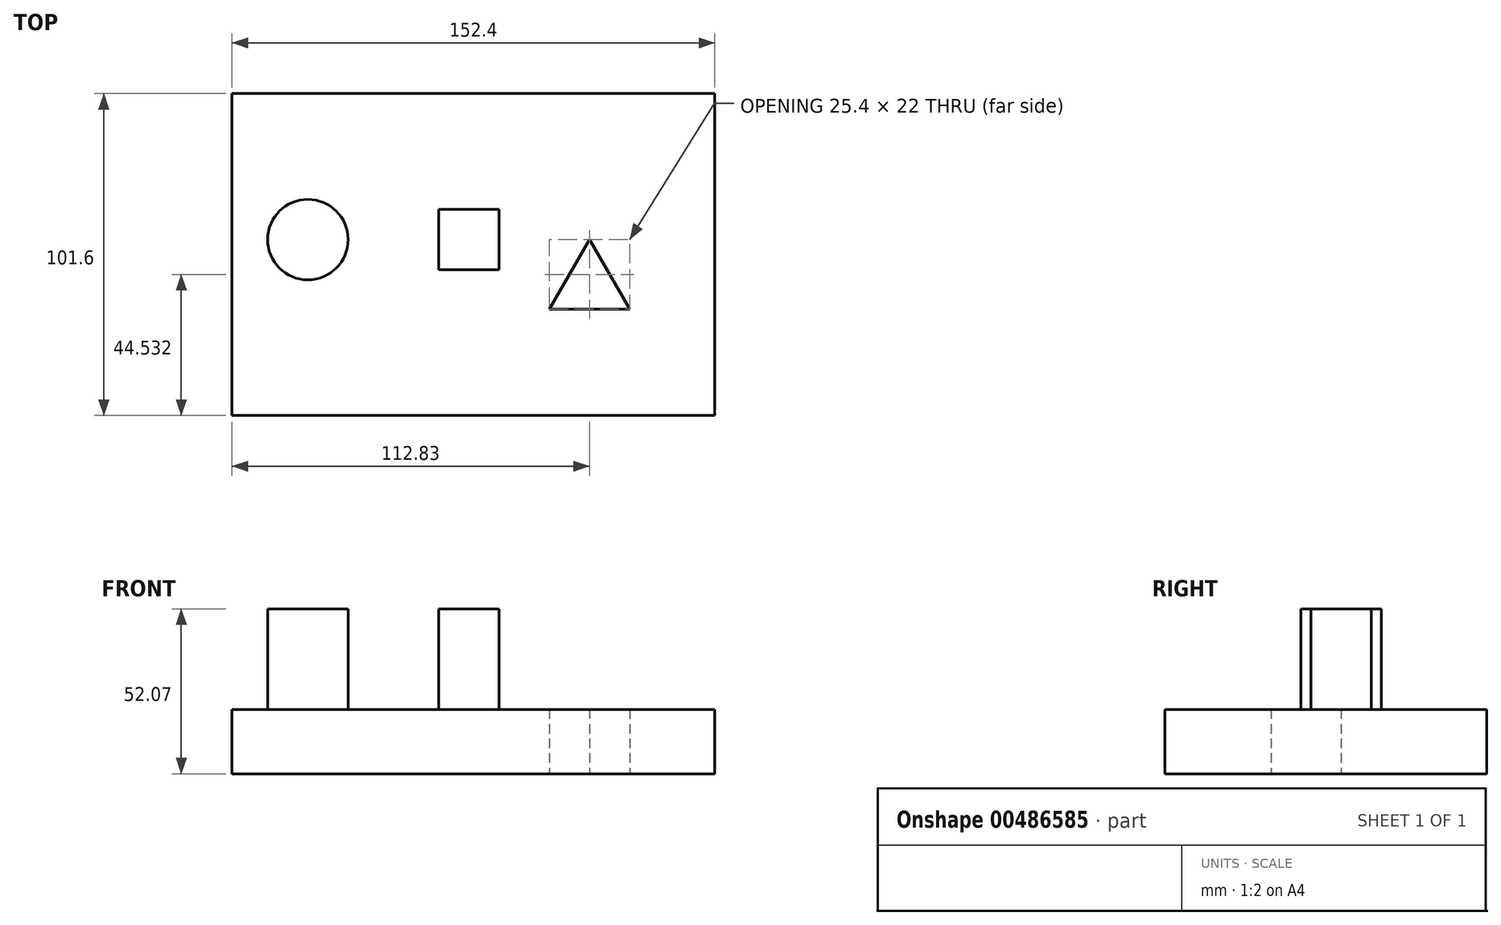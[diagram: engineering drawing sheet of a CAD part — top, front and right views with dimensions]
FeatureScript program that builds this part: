
annotation { "Feature Type Name" : "Feature", "Feature Type Description" : "" }
export const myFeature = defineFeature(function(context is Context, id is Id, definition is map)
    precondition{}
    {
        {
            var Q0;
            Q0=qCreatedBy(makeId("Top.planeOp"),FACE);
            var sketch = newSketch(context, id + "F0", { "sketchPlane" : qUnion([Q0])});
            skLineSegment(sketch, "E0", {"start": v(0, 0) * mm, "end": v(6.35, 0) * mm});
            skLineSegment(sketch, "E1", {"start": v(6.35, 0) * mm, "end": v(-6.35, -22) * mm});
            skLineSegment(sketch, "E2", {"start": v(-6.35, -22) * mm, "end": v(19.05, -22) * mm});
            skLineSegment(sketch, "E3", {"start": v(19.05, -22) * mm, "end": v(6.35, 0) * mm});
            skLineSegment(sketch, "E4", {"start": v(0, 0) * mm, "end": v(-31.75, 0) * mm});
            skLineSegment(sketch, "E5.bottom", {"start": v(-22.22, 9.53) * mm, "end": v(-41.27, 9.53) * mm});
            skLineSegment(sketch, "E5.top", {"start": v(-22.22, -9.53) * mm, "end": v(-41.28, -9.52) * mm});
            skLineSegment(sketch, "E5.left", {"start": v(-22.22, 9.53) * mm, "end": v(-22.23, -9.53) * mm});
            skLineSegment(sketch, "E5.right", {"start": v(-41.27, 9.53) * mm, "end": v(-41.27, -9.52) * mm});
            skPoint(sketch, "E5.middle", {"position": v(-31.75, 0) * mm});
            skLineSegment(sketch, "E6", {"start": v(-31.75, 0) * mm, "end": v(-82.55, 0) * mm});
            skCircle(sketch, "E7", {"center": v(-82.55, 0) * mm, "radius": 12.7 * mm});
            skLineSegment(sketch, "E8.bottom", {"start": v(-106.48, 46.07) * mm, "end": v(45.92, 46.07) * mm});
            skLineSegment(sketch, "E8.top", {"start": v(-106.48, -55.53) * mm, "end": v(45.92, -55.53) * mm});
            skLineSegment(sketch, "E8.left", {"start": v(-106.48, 46.07) * mm, "end": v(-106.48, -55.53) * mm});
            skLineSegment(sketch, "E8.right", {"start": v(45.92, 46.07) * mm, "end": v(45.92, -55.53) * mm});
            skSolve(sketch);
        }
        {
            var Q0;
            Q0 = qSketchRegion(id + "F0", true);
            extrude(context, id + "F1", {"entities" : qUnion([Q0]), "depth" : 20.32 * mm});
        }
        {
            var Q0;
            {var subQ1=sQuery(id+"F0.wireOp",EDGE,"E5.top");Q0=makeQuery(id+"F0.imprint","IMPRINT",FACE,{"disambiguationData":[TD([[makeQuery(id+"F0.imprint","IMPRINT",EDGE,{"derivedFrom":subQ1}),-1.0]])]});}
            var Q1;
            {var subQ1=sQuery(id+"F0.wireOp",EDGE,"E5.bottom");Q1=makeQuery(id+"F0.imprint","IMPRINT",FACE,{"disambiguationData":[TD([[makeQuery(id+"F0.imprint","IMPRINT",EDGE,{"derivedFrom":subQ1}),1.0]])]});}
            extrude(context, id + "F2", {"entities" : qUnion([Q0, Q1]), "operationType" : NewBodyOperationType.ADD, "depth" : 52.07 * mm});
        }
        {
            var Q0;
            Q0=makeQuery(id+"F0.imprint","IMPRINT",FACE,{"disambiguationData":[TD([[makeQuery(id+"F0.imprint","IMPRINT",EDGE,{"derivedFrom":sQuery(id+"F0.wireOp",EDGE,"E7")}),1.0]])]});
            extrude(context, id + "F3", {"entities" : qUnion([Q0]), "operationType" : NewBodyOperationType.ADD, "depth" : 52.07 * mm});
        }
    });
